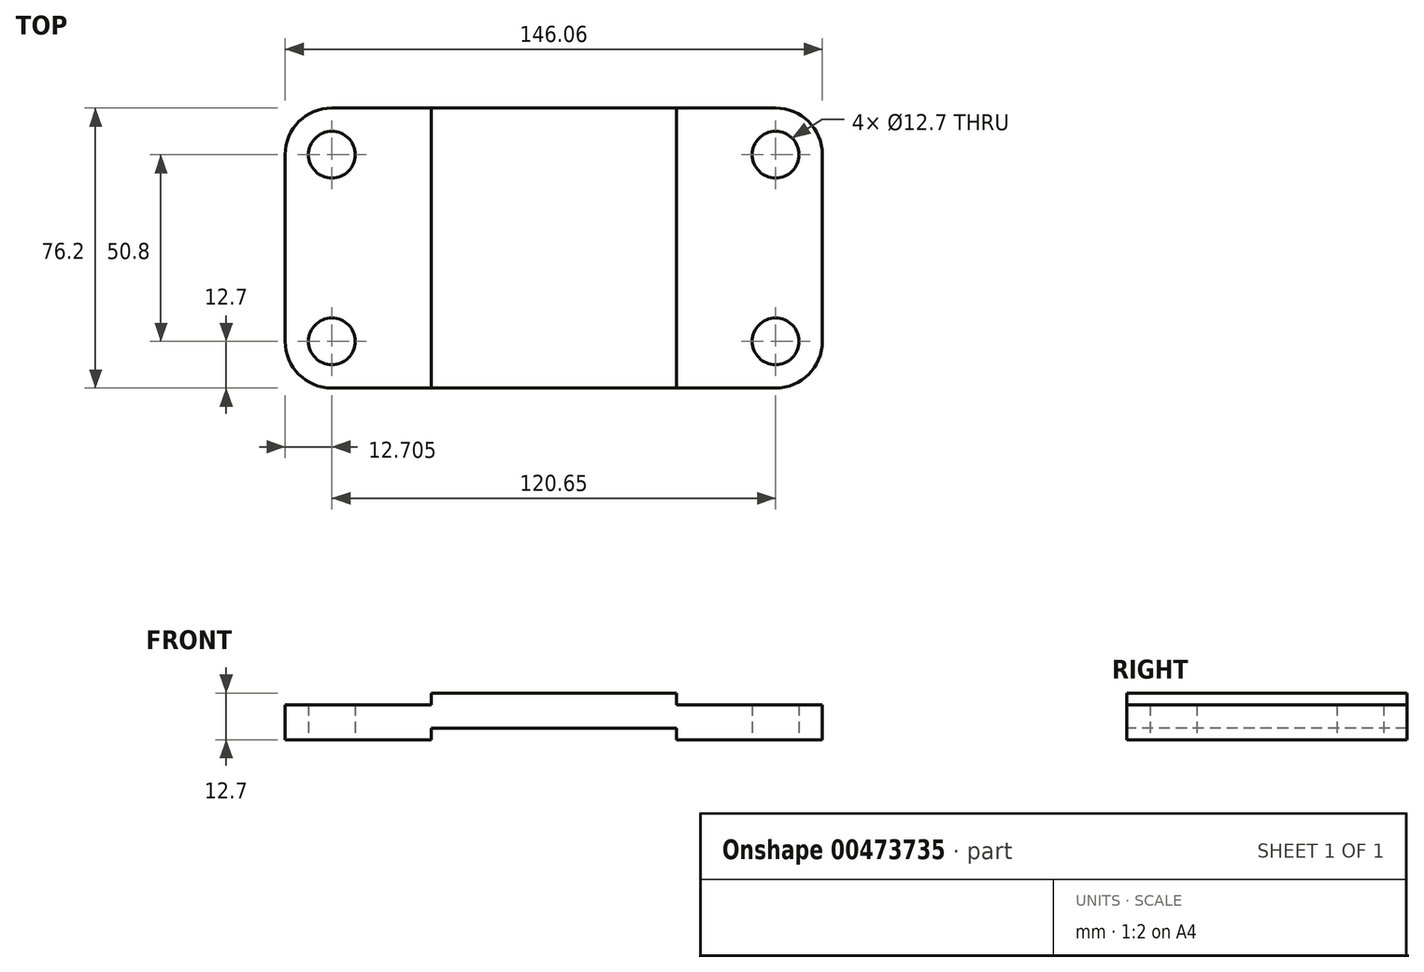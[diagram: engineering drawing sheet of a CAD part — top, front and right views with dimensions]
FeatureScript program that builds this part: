
annotation { "Feature Type Name" : "Feature", "Feature Type Description" : "" }
export const myFeature = defineFeature(function(context is Context, id is Id, definition is map)
    precondition{}
    {
        {
            var Q0;
            Q0=qCreatedBy(makeId("Top.planeOp"),FACE);
            var sketch = newSketch(context, id + "F0", { "sketchPlane" : qUnion([Q0])});
            skLineSegment(sketch, "E0.bottom", {"start": v(-60.33, 25.4) * mm, "end": v(60.33, 25.4) * mm});
            skLineSegment(sketch, "E0.top", {"start": v(-60.33, -25.4) * mm, "end": v(60.33, -25.4) * mm});
            skLineSegment(sketch, "E0.left", {"start": v(-60.33, 25.4) * mm, "end": v(-60.33, -25.4) * mm});
            skLineSegment(sketch, "E0.right", {"start": v(60.33, 25.4) * mm, "end": v(60.33, -25.4) * mm});
            skPoint(sketch, "E0.middle", {"position": v(0, 0) * mm});
            skLineSegment(sketch, "E1.bottom", {"start": v(-73.03, 38.1) * mm, "end": v(73.03, 38.1) * mm});
            skLineSegment(sketch, "E1.top", {"start": v(-73.03, -38.1) * mm, "end": v(73.03, -38.1) * mm});
            skLineSegment(sketch, "E1.left", {"start": v(-73.03, 38.1) * mm, "end": v(-73.03, -38.1) * mm});
            skLineSegment(sketch, "E1.right", {"start": v(73.03, 38.1) * mm, "end": v(73.03, -38.1) * mm});
            skCircle(sketch, "E2", {"center": v(-60.33, 25.4) * mm, "radius": 6.35 * mm});
            skCircle(sketch, "E3", {"center": v(-60.33, -25.4) * mm, "radius": 6.35 * mm});
            skCircle(sketch, "E4", {"center": v(60.33, -25.4) * mm, "radius": 6.35 * mm});
            skCircle(sketch, "E5", {"center": v(60.33, 25.4) * mm, "radius": 6.35 * mm});
            skSolve(sketch);
        }
        {
            var Q0;
            {var subQ5=sQuery(id+"F0.wireOp",EDGE,"E2");var subQ13=sQuery(id+"F0.wireOp",EDGE,"E0.bottom");var subQ14=makeQuery(id+"F0.imprint","INTERSECT",VERTEX,{"derivedFrom":[subQ13,subQ5]});Q0=makeQuery(id+"F0.imprint","IMPRINT",FACE,{"disambiguationData":[TD([[makeQuery(id+"F0.imprint","IMPRINT",EDGE,{"disambiguationData":[TD([[subQ14,-1.0]])],"derivedFrom":subQ13}),-1.0]])]});}
            var Q1;
            Q1=makeQuery(id+"F0.imprint","IMPRINT",FACE,{"disambiguationData":[TD([[makeQuery(id+"F0.imprint","IMPRINT",EDGE,{"derivedFrom":sQuery(id+"F0.wireOp",EDGE,"E1.bottom")}),-1.0]])]});
            extrude(context, id + "F1", {"entities" : qUnion([Q0, Q1]), "depth" : 9.52 * mm});
        }
        {
            var Q0;
            Q0=makeQuery(id+"F1.opExtrude","SWEPT_EDGE",EDGE,{"disambiguationData":[OSD([sQuery(id+"F0.wireOp",EDGE,"E1.top"),sQuery(id+"F0.wireOp",EDGE,"E1.left")])]});
            var Q1;
            Q1=makeQuery(id+"F1.opExtrude","SWEPT_EDGE",EDGE,{"disambiguationData":[OSD([sQuery(id+"F0.wireOp",EDGE,"E1.bottom"),sQuery(id+"F0.wireOp",EDGE,"E1.left")])]});
            var Q2;
            Q2=makeQuery(id+"F1.opExtrude","SWEPT_EDGE",EDGE,{"disambiguationData":[OSD([sQuery(id+"F0.wireOp",EDGE,"E1.bottom"),sQuery(id+"F0.wireOp",EDGE,"E1.right")])]});
            var Q3;
            Q3=makeQuery(id+"F1.opExtrude","SWEPT_EDGE",EDGE,{"disambiguationData":[OSD([sQuery(id+"F0.wireOp",EDGE,"E1.top"),sQuery(id+"F0.wireOp",EDGE,"E1.right")])]});
            fillet(context, id + "F2", {"entities" : qUnion([Q0, Q1, Q2, Q3]), "radius" : 12.7 * mm, "tangentPropagation" : true, "allowEdgeOverflow" : false});
        }
        {
            var Q0;
            Q0=makeQuery(id+"F1.opExtrude","CAP_FACE",FACE,{"disambiguationData":[OSD([sQuery(id+"F0.wireOp",EDGE,"E1.bottom"),sQuery(id+"F0.wireOp",EDGE,"E1.top"),sQuery(id+"F0.wireOp",EDGE,"E1.left"),sQuery(id+"F0.wireOp",EDGE,"E1.right"),sQuery(id+"F0.wireOp",EDGE,"E2"),sQuery(id+"F0.wireOp",EDGE,"E3"),sQuery(id+"F0.wireOp",EDGE,"E4"),sQuery(id+"F0.wireOp",EDGE,"E5")])],"isStart":false});
            var sketch = newSketch(context, id + "F3", { "sketchPlane" : qUnion([Q0])});
            skLineSegment(sketch, "E6.bottom", {"start": v(-33.34, -38.1) * mm, "end": v(33.34, -38.1) * mm});
            skLineSegment(sketch, "E6.top", {"start": v(-33.34, 38.1) * mm, "end": v(33.34, 38.1) * mm});
            skLineSegment(sketch, "E6.left", {"start": v(-33.34, -38.1) * mm, "end": v(-33.34, 38.1) * mm});
            skLineSegment(sketch, "E6.right", {"start": v(33.34, -38.1) * mm, "end": v(33.34, 38.1) * mm});
            skPoint(sketch, "E6.middle", {"position": v(0, 0) * mm});
            skSolve(sketch);
        }
        {
            var Q0;
            Q0=makeQuery(id+"F3.imprint","IMPRINT",FACE,{"disambiguationData":[TD([[makeQuery(id+"F3.imprint","IMPRINT",EDGE,{"derivedFrom":sQuery(id+"F3.wireOp",EDGE,"E6.bottom")}),1.0]])]});
            extrude(context, id + "F4", {"entities" : qUnion([Q0]), "operationType" : NewBodyOperationType.ADD, "depth" : 3.17 * mm});
        }
        {
            var Q0;
            {var subQ5=sQuery(id+"F0.wireOp",EDGE,"E2");var subQ13=sQuery(id+"F0.wireOp",EDGE,"E0.bottom");var subQ14=makeQuery(id+"F0.imprint","INTERSECT",VERTEX,{"derivedFrom":[subQ13,subQ5]});Q0=makeQuery(id+"F0.imprint","IMPRINT",FACE,{"disambiguationData":[TD([[makeQuery(id+"F0.imprint","IMPRINT",EDGE,{"disambiguationData":[TD([[subQ14,-1.0]])],"derivedFrom":subQ13}),-1.0]])]});}
            var sketch = newSketch(context, id + "F5", { "sketchPlane" : qUnion([Q0])});
            skLineSegment(sketch, "E7.bottom", {"start": v(-33.34, 38.1) * mm, "end": v(33.34, 38.1) * mm});
            skLineSegment(sketch, "E7.top", {"start": v(-33.34, -38.1) * mm, "end": v(33.34, -38.1) * mm});
            skLineSegment(sketch, "E7.left", {"start": v(-33.34, 38.1) * mm, "end": v(-33.34, -38.1) * mm});
            skLineSegment(sketch, "E7.right", {"start": v(33.34, 38.1) * mm, "end": v(33.34, -38.1) * mm});
            skPoint(sketch, "E7.middle", {"position": v(0, 0) * mm});
            skSolve(sketch);
        }
        {
            var Q0;
            {var subQ0=sQuery(id+"F5.wireOp",EDGE,"E7.bottom");Q0=makeQuery(id+"F5.imprint","IMPRINT",FACE,{"disambiguationData":[TD([[makeQuery(id+"F5.imprint","IMPRINT",EDGE,{"derivedFrom":subQ0}),-1.0]])]});}
            var Q1;
            {var subQ0=sQuery(id+"F5.wireOp",EDGE,"E7.left");var subQ1=sQuery(id+"F0.wireOp",EDGE,"E0.bottom");var subQ2=makeQuery(id+"F0.imprint","IMPRINT",EDGE,{"disambiguationData":[TD([[makeQuery(id+"F0.imprint","INTERSECT",VERTEX,{"derivedFrom":[subQ1,sQuery(id+"F0.wireOp",EDGE,"E2")]}),-1.0]])],"derivedFrom":subQ1});var subQ3=makeQuery(id+"F5.imprint","INTERSECT",VERTEX,{"derivedFrom":[subQ2,subQ0]});Q1=makeQuery(id+"F5.imprint","IMPRINT",FACE,{"disambiguationData":[TD([[makeQuery(id+"F5.imprint","IMPRINT",EDGE,{"disambiguationData":[TD([[subQ3,-1.0]])],"derivedFrom":subQ0}),1.0]])]});}
            var Q2;
            {var subQ0=sQuery(id+"F5.wireOp",EDGE,"E7.top");Q2=makeQuery(id+"F5.imprint","IMPRINT",FACE,{"disambiguationData":[TD([[makeQuery(id+"F5.imprint","IMPRINT",EDGE,{"derivedFrom":subQ0}),1.0]])]});}
            extrude(context, id + "F6", {"entities" : qUnion([Q0, Q1, Q2]), "operationType" : NewBodyOperationType.REMOVE, "depth" : 3.17 * mm});
        }
    });
